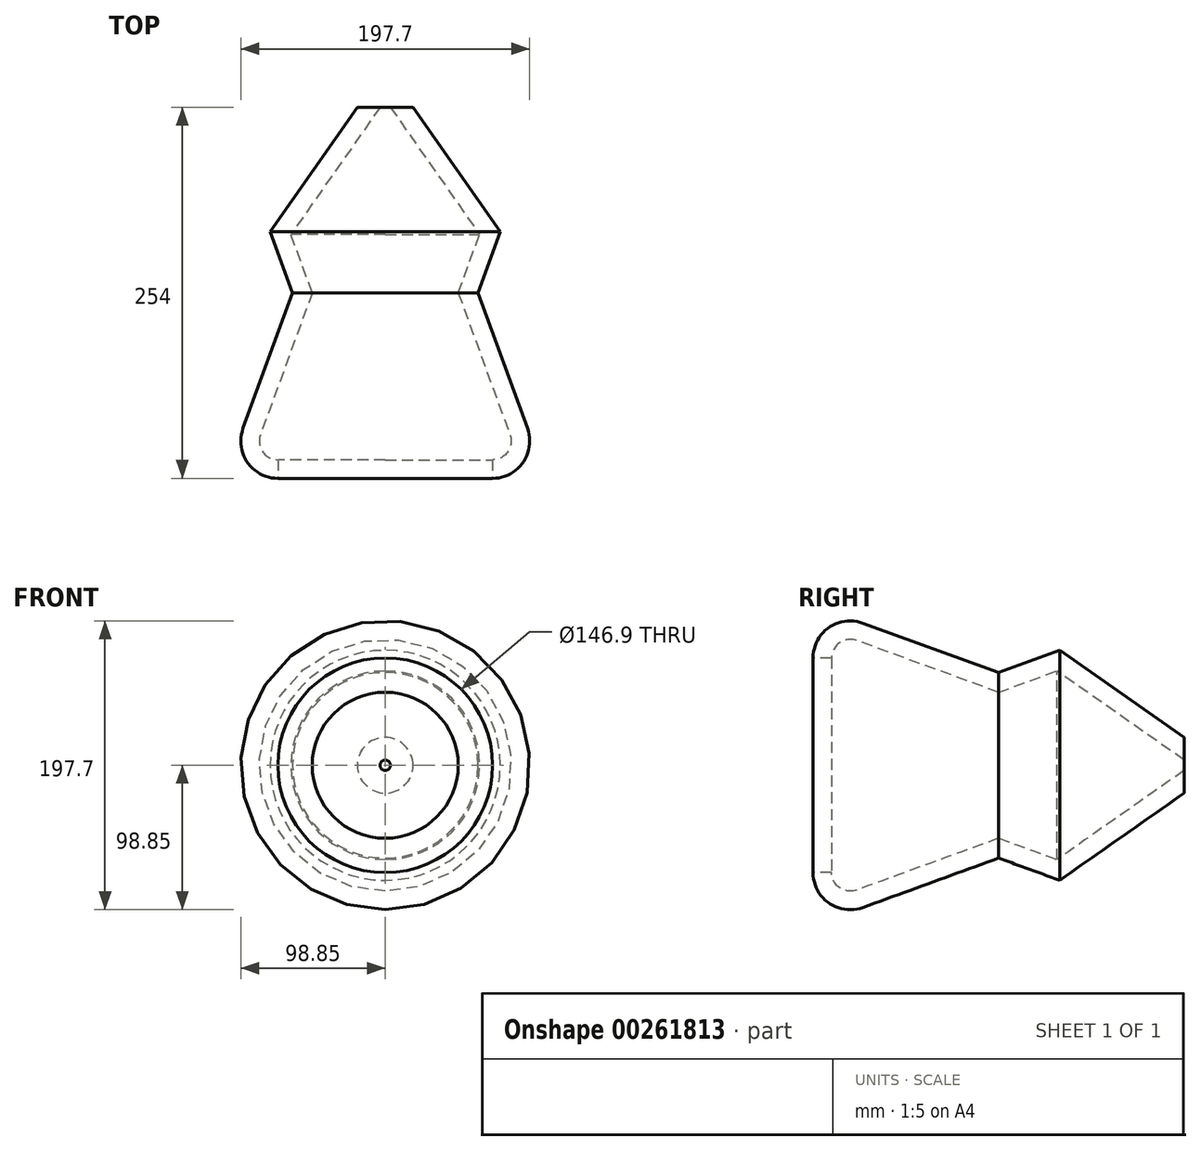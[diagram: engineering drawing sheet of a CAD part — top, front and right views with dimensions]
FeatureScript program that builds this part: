
annotation { "Feature Type Name" : "Feature", "Feature Type Description" : "" }
export const myFeature = defineFeature(function(context is Context, id is Id, definition is map)
    precondition{}
    {
        {
            var Q0;
            Q0=qCreatedBy(makeId("Front.planeOp"),FACE);
            var sketch = newSketch(context, id + "F0", { "sketchPlane" : qUnion([Q0])});
            skCircle(sketch, "E0", {"center": v(0, 0) * mm, "radius": 63.5 * mm});
            skSolve(sketch);
        }
        {
            var Q0;
            Q0=makeQuery(id+"F0.imprint","IMPRINT",FACE,{"disambiguationData":[TD([[makeQuery(id+"F0.imprint","IMPRINT",EDGE,{"derivedFrom":sQuery(id+"F0.wireOp",EDGE,"E0")}),1.0]])]});
            extrude(context, id + "F1", {"entities" : qUnion([Q0]), "endBound" : BoundingType.SYMMETRIC, "depth" : 254 * mm, "hasDraft" : true, "draftAngle" : 20 * degree});
        }
        {
            var Q0;
            Q0=makeQuery(id+"F1.opExtrude","CAP_EDGE",EDGE,{"disambiguationData":[OSD([sQuery(id+"F0.wireOp",EDGE,"E0")])],"isStart":false});
            fillet(context, id + "F2", {"entities" : qUnion([Q0]), "radius" : 25.4 * mm, "tangentPropagation" : true, "allowEdgeOverflow" : false});
        }
        {
            var Q0;
            Q0=makeQuery(id+"F1.opExtrude","CAP_EDGE",EDGE,{"disambiguationData":[OSD([sQuery(id+"F0.wireOp",EDGE,"E0")])],"isStart":true});
            chamfer(context, id + "F3", {"entities" : qUnion([Q0]), "width" : 63.5 * mm});
        }
        {
            var Q0;
            Q0=makeQuery(id+"F1.opExtrude","CAP_FACE",FACE,{"disambiguationData":[OSD([sQuery(id+"F0.wireOp",EDGE,"E0")])],"isStart":false});
            var Q1;
            Q1=makeQuery(id+"F1.opExtrude","CAP_FACE",FACE,{"disambiguationData":[OSD([sQuery(id+"F0.wireOp",EDGE,"E0")])],"isStart":true});
            shell(context, id + "F4", {"entities" : qUnion([Q0, Q1]), "thickness" : 12.7 * mm});
        }
    });
